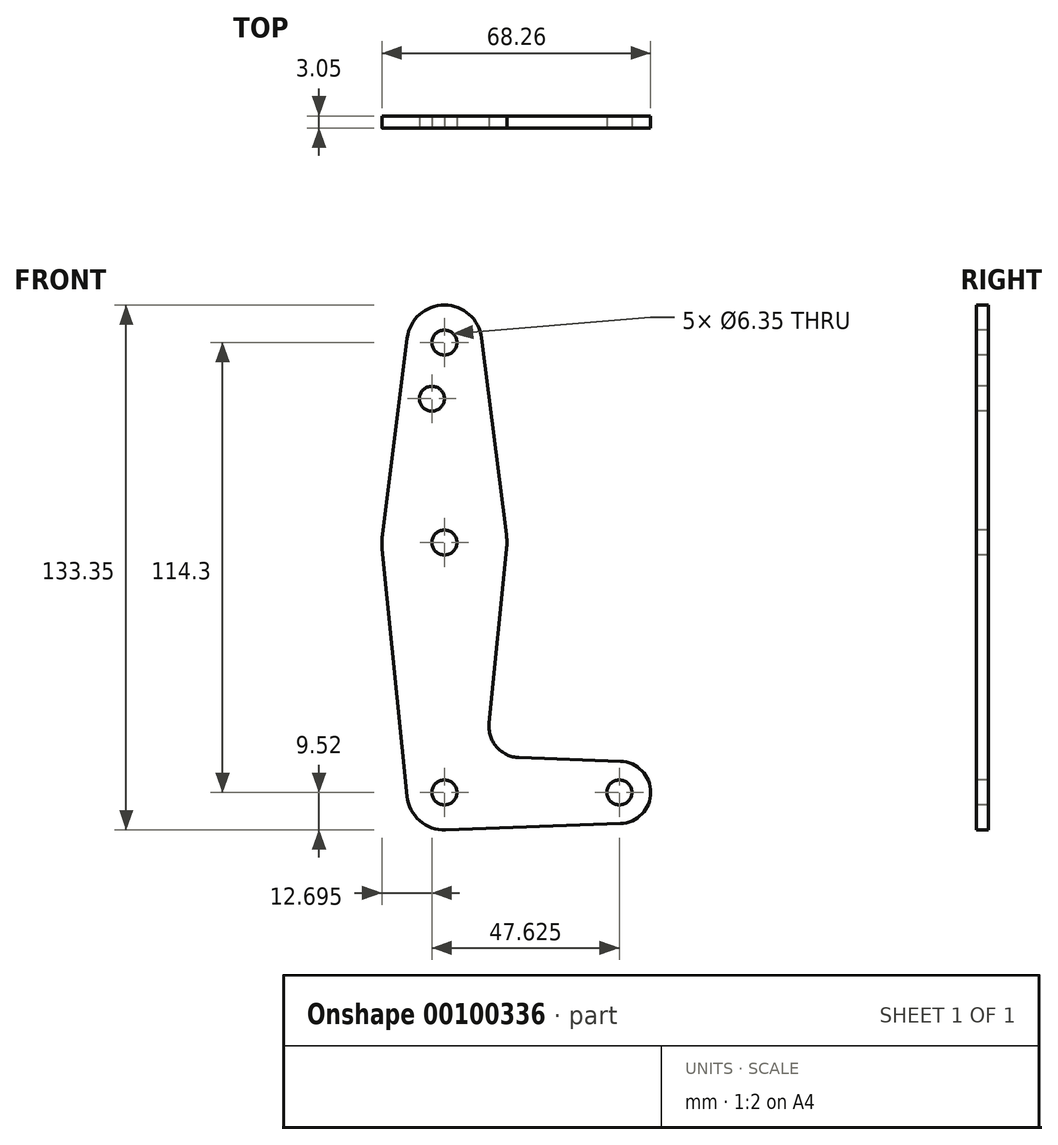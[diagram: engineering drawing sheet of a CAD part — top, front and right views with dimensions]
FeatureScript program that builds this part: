
annotation { "Feature Type Name" : "Feature", "Feature Type Description" : "" }
export const myFeature = defineFeature(function(context is Context, id is Id, definition is map)
    precondition{}
    {
        {
            var Q0;
            Q0=qCreatedBy(makeId("Front.planeOp"),FACE);
            var sketch = newSketch(context, id + "F0", { "sketchPlane" : qUnion([Q0])});
            skLineSegment(sketch, "E0", {"start": v(0, 114.3) * mm, "end": v(0, 0) * mm, "construction": true});
            skLineSegment(sketch, "E1", {"start": v(0, 0) * mm, "end": v(44.45, 0) * mm, "construction": true});
            skCircle(sketch, "E2", {"center": v(0, 114.3) * mm, "radius": 9.53 * mm});
            skCircle(sketch, "E3", {"center": v(0, 63.5) * mm, "radius": 15.88 * mm});
            skCircle(sketch, "E4", {"center": v(0, 0) * mm, "radius": 9.53 * mm});
            skCircle(sketch, "E5", {"center": v(44.45, 0) * mm, "radius": 7.94 * mm});
            skLineSegment(sketch, "E6", {"start": v(-9.45, 115.5) * mm, "end": v(-15.75, 65.48) * mm});
            skLineSegment(sketch, "E7", {"start": v(-15.8, 61.91) * mm, "end": v(-9.48, -0.95) * mm});
            skLineSegment(sketch, "E8", {"start": v(9.45, 115.5) * mm, "end": v(15.75, 65.48) * mm});
            skLineSegment(sketch, "E9", {"start": v(15.8, 61.91) * mm, "end": v(11.34, 17.6) * mm});
            skLineSegment(sketch, "E10", {"start": v(18.97, 8.85) * mm, "end": v(44.73, 7.93) * mm});
            skLineSegment(sketch, "E11", {"start": v(0.34, -9.52) * mm, "end": v(44.73, -7.93) * mm});
            skCircle(sketch, "E12", {"center": v(0, 114.3) * mm, "radius": 3.18 * mm});
            skCircle(sketch, "E13", {"center": v(-3.18, 100.03) * mm, "radius": 3.18 * mm});
            skCircle(sketch, "E14", {"center": v(0, 63.5) * mm, "radius": 3.18 * mm});
            skCircle(sketch, "E15", {"center": v(0, 0) * mm, "radius": 3.18 * mm});
            skCircle(sketch, "E16", {"center": v(44.45, 0) * mm, "radius": 3.18 * mm});
            skArc(sketch, "E17.filletArc", {"start": v(11.34, 17.6) * mm, "mid": v(13.26, 11.57) * mm, "end": v(18.97, 8.85) * mm});
            skSolve(sketch);
        }
        {
            var Q0;
            Q0=makeQuery(id+"F0.imprint","IMPRINT",FACE,{"disambiguationData":[TD([[makeQuery(id+"F0.imprint","IMPRINT",EDGE,{"derivedFrom":sQuery(id+"F0.wireOp",EDGE,"E12")}),-1.0]])]});
            var Q1;
            Q1=makeQuery(id+"F0.imprint","IMPRINT",FACE,{"disambiguationData":[TD([[makeQuery(id+"F0.imprint","IMPRINT",EDGE,{"derivedFrom":sQuery(id+"F0.wireOp",EDGE,"E15")}),-1.0]])]});
            var Q2;
            Q2=makeQuery(id+"F0.imprint","IMPRINT",FACE,{"disambiguationData":[TD([[makeQuery(id+"F0.imprint","IMPRINT",EDGE,{"derivedFrom":sQuery(id+"F0.wireOp",EDGE,"E16")}),-1.0]])]});
            var Q3;
            Q3=makeQuery(id+"F0.imprint","IMPRINT",FACE,{"disambiguationData":[TD([[makeQuery(id+"F0.imprint","IMPRINT",EDGE,{"derivedFrom":sQuery(id+"F0.wireOp",EDGE,"E14")}),-1.0]])]});
            var Q4;
            {var subQ0=sQuery(id+"F0.wireOp",EDGE,"E7");Q4=makeQuery(id+"F0.imprint","IMPRINT",FACE,{"disambiguationData":[TD([[makeQuery(id+"F0.imprint","IMPRINT",EDGE,{"derivedFrom":subQ0}),1.0]])]});}
            var Q5;
            {var subQ1=sQuery(id+"F0.wireOp",EDGE,"E6");Q5=makeQuery(id+"F0.imprint","IMPRINT",FACE,{"disambiguationData":[TD([[makeQuery(id+"F0.imprint","IMPRINT",EDGE,{"derivedFrom":subQ1}),1.0]])]});}
            extrude(context, id + "F1", {"entities" : qUnion([Q0, Q1, Q2, Q3, Q4, Q5]), "oppositeDirection" : true, "depth" : 3.05 * mm});
        }
    });
